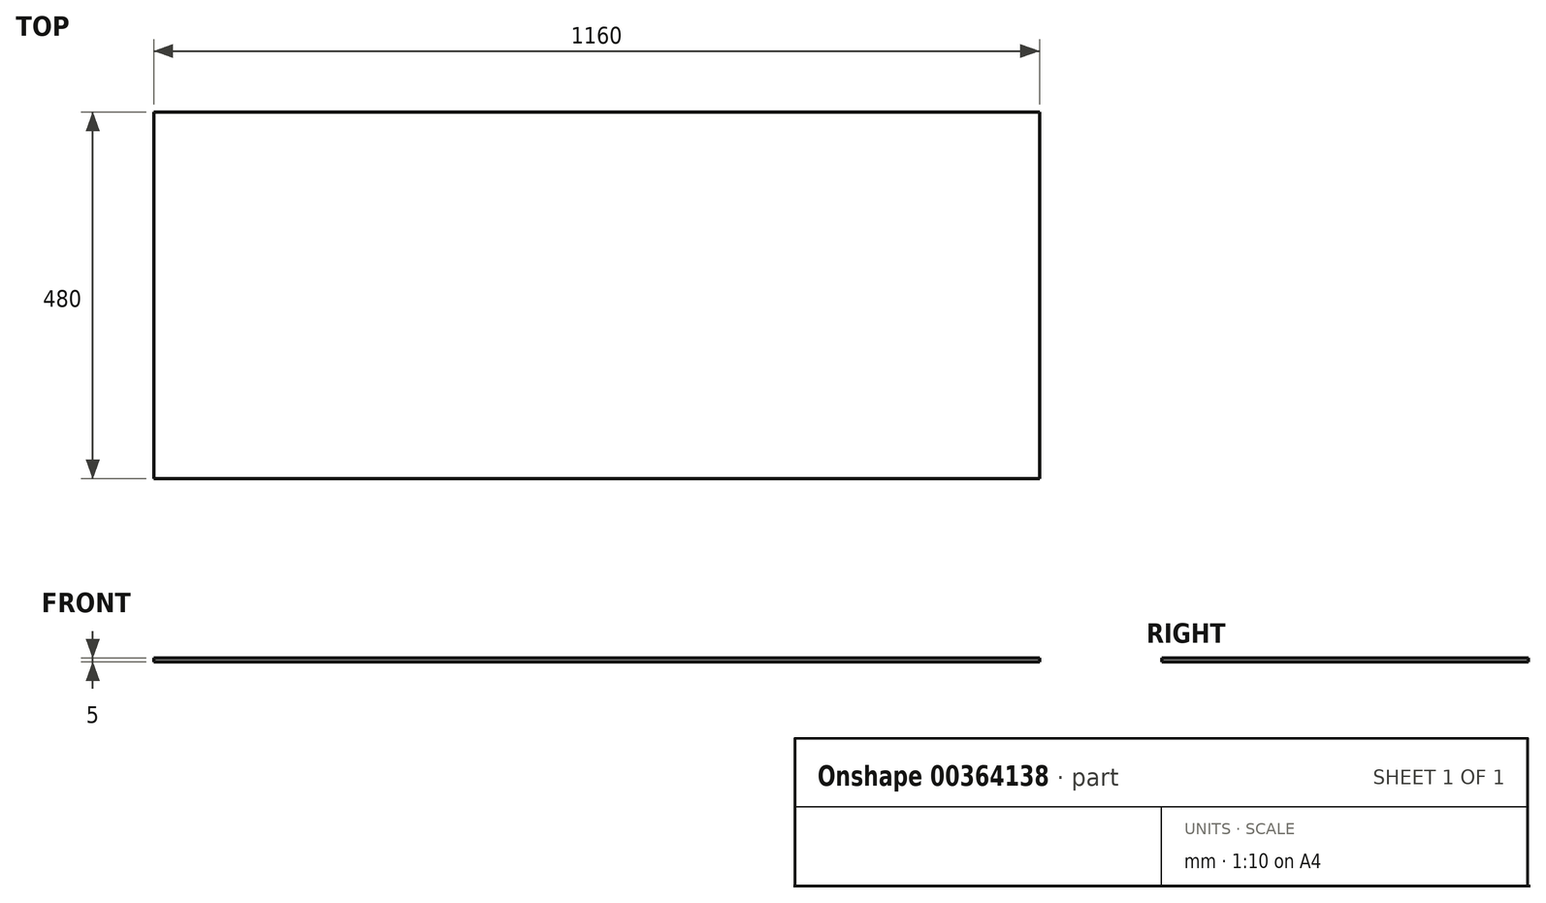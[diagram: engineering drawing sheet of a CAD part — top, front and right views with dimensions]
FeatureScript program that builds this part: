
annotation { "Feature Type Name" : "Feature", "Feature Type Description" : "" }
export const myFeature = defineFeature(function(context is Context, id is Id, definition is map)
    precondition{}
    {
        {
            var Q0;
            Q0=qCreatedBy(makeId("Top.planeOp"),FACE);
            var sketch = newSketch(context, id + "F0", { "sketchPlane" : qUnion([Q0])});
            skLineSegment(sketch, "E0.bottom", {"start": v(-580, 0) * mm, "end": v(580, 0) * mm});
            skLineSegment(sketch, "E0.top", {"start": v(-580, 480) * mm, "end": v(580, 480) * mm});
            skLineSegment(sketch, "E0.left", {"start": v(-580, 0) * mm, "end": v(-580, 480) * mm});
            skLineSegment(sketch, "E0.right", {"start": v(580, 0) * mm, "end": v(580, 480) * mm});
            skSolve(sketch);
        }
        {
            var Q0;
            Q0=makeQuery(id+"F0.imprint","IMPRINT",FACE,{"disambiguationData":[TD([[makeQuery(id+"F0.imprint","IMPRINT",EDGE,{"derivedFrom":sQuery(id+"F0.wireOp",EDGE,"E0.bottom")}),1.0]])]});
            extrude(context, id + "F1", {"entities" : qUnion([Q0]), "depth" : 5 * mm});
        }
    });
